# Revit family: Casement no trim w transom
name_source: partatom
category: Windows
revit_build: Autodesk Revit Architecture 2015 (Build: 20140323_1530(x64)
units: mm (PartAtom-declared; Revit-internal decimal feet)

## types (11) — shared parameters
Analytic Construction = <None>
Frame Thickness = 0' - 2"
Glass Material = Glass
Trim Projection = 0' - 1"
Trim Width = 0' - 3"
Wall Closure = By host

## per-type parameters (varying)
| type | Default Sill Height | Frame Material | Height | Sash Material | Tansom Height | Width |
| 36" x 48" | 3' - 0" | Frame Material | 4' - 0" | Trim Material | 1' - 2" | 3' - 0" |
| 24" x 36" | 4' - 0" | Frame Material | 3' - 0" | Trim Material | 1' - 2" | 2' - 0" |
| 36" x 60" | 2' - 0" | Wood | 5' - 0" | Wood | 1' - 8" | 3' - 0" |
| 42" x 60" | 2' - 0" | Wood | 5' - 0" | Wood | 1' - 2" | 3' - 6" |
| 32" x 60" | 4' - 0" | Wood | 5' - 0" | Wood | 1' - 8" | 2' - 8" |
| 38" x 60" | 2' - 0" | Wood | 5' - 0" | Wood | 1' - 8" | 3' - 2" |
| 54" x 60" | 2' - 0" | Wood | 5' - 0" | Wood | 1' - 8" | 4' - 6" |
| 24" x 60" | 3' - 1" | Wood | 5' - 0" | Wood | 1' - 8" | 2' - 0" |
| 30" x 60" | 4' - 0" | Wood | 5' - 0" | Wood | 2' - 6" | 2' - 6" |
| 30" x 72" | 4' - 0" | Wood | 6' - 0" | Wood | 3' - 0" | 2' - 6" |
| 30" x 84" | 4' - 0" | Wood | 7' - 0" | Wood | 5' - 0" | 2' - 6" |

## geometry (parser evidence)
native form markers: Blend x4, Sweep x1
no freeform markers — native parametric forms only
